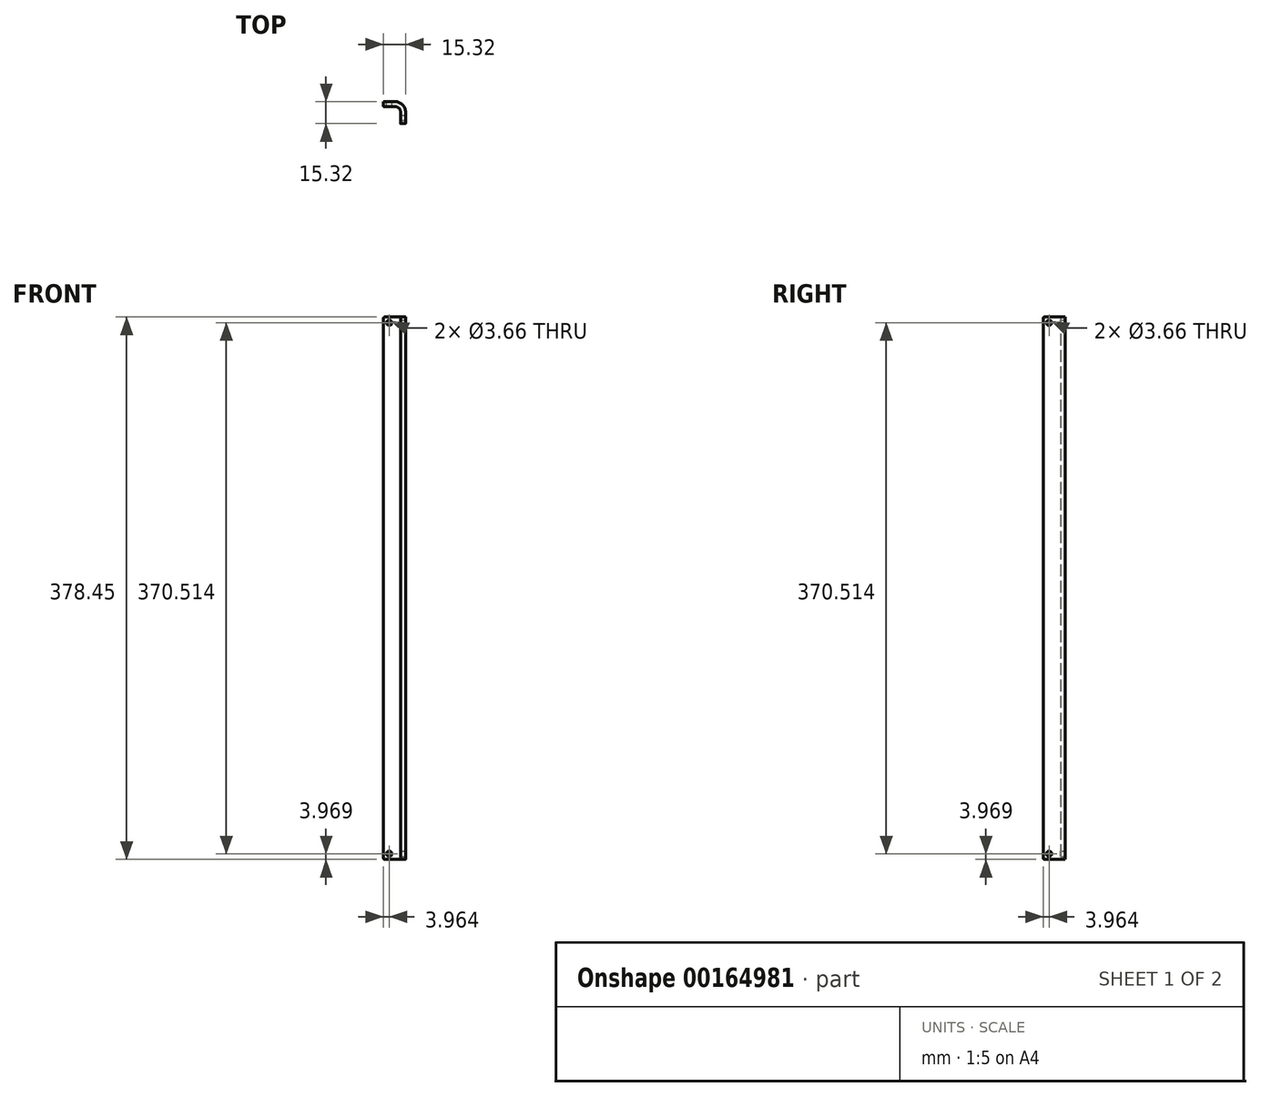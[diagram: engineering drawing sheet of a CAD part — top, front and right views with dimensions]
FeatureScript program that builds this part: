
annotation { "Feature Type Name" : "Feature", "Feature Type Description" : "" }
export const myFeature = defineFeature(function(context is Context, id is Id, definition is map)
    precondition{}
    {
        {
            var Q0;
            Q0=qCreatedBy(makeId("Top.planeOp"),FACE);
            var sketch = newSketch(context, id + "F0", { "sketchPlane" : qUnion([Q0])});
            skLineSegment(sketch, "E0.bottom", {"start": v(0, 0) * mm, "end": v(-11.9, 0) * mm});
            skLineSegment(sketch, "E0.top", {"start": v(3.42, 3.42) * mm, "end": v(-11.9, 3.42) * mm});
            skLineSegment(sketch, "E0.right", {"start": v(-11.9, 0) * mm, "end": v(-11.9, 3.42) * mm});
            skLineSegment(sketch, "E1.top", {"start": v(0, -11.9) * mm, "end": v(3.42, -11.9) * mm});
            skLineSegment(sketch, "E1.left", {"start": v(0, 0) * mm, "end": v(0, -11.9) * mm});
            skLineSegment(sketch, "E1.right", {"start": v(3.42, 3.42) * mm, "end": v(3.42, -11.9) * mm});
            skSolve(sketch);
        }
        {
            var Q0;
            Q0 = qSketchRegion(id + "F0", true);
            extrude(context, id + "F1", {"entities" : qUnion([Q0]), "depth" : 378.45 * mm});
        }
        {
            var Q0;
            Q0=makeQuery(id+"F1.opExtrude","SWEPT_EDGE",EDGE,{"disambiguationData":[OSD([sQuery(id+"F0.wireOp",EDGE,"E0.bottom"),sQuery(id+"F0.wireOp",EDGE,"E1.left")])]});
            fillet(context, id + "F2", {"entities" : qUnion([Q0]), "radius" : 3.97 * mm, "tangentPropagation" : true, "allowEdgeOverflow" : false});
        }
        {
            var Q0;
            Q0=makeQuery(id+"F1.opExtrude","SWEPT_EDGE",EDGE,{"disambiguationData":[OSD([sQuery(id+"F0.wireOp",EDGE,"E0.top"),sQuery(id+"F0.wireOp",EDGE,"E1.right")])]});
            fillet(context, id + "F3", {"entities" : qUnion([Q0]), "radius" : 7.39 * mm, "tangentPropagation" : true, "allowEdgeOverflow" : false});
        }
        {
            var Q0;
            Q0=makeQuery(id+"F1.opExtrude","SWEPT_FACE",FACE,{"disambiguationData":[OSD([sQuery(id+"F0.wireOp",EDGE,"E0.top")])]});
            var sketch = newSketch(context, id + "F4", { "sketchPlane" : qUnion([Q0])});
            skLineSegment(sketch, "E2.bottom", {"start": v(7.94, 378.45) * mm, "end": v(11.9, 378.45) * mm, "construction": true});
            skLineSegment(sketch, "E2.top", {"start": v(7.94, 374.48) * mm, "end": v(11.9, 374.48) * mm, "construction": true});
            skLineSegment(sketch, "E2.left", {"start": v(7.94, 378.45) * mm, "end": v(7.94, 374.48) * mm, "construction": true});
            skLineSegment(sketch, "E2.right", {"start": v(11.9, 378.45) * mm, "end": v(11.9, 374.48) * mm, "construction": true});
            skLineSegment(sketch, "E3.bottom", {"start": v(7.94, 0) * mm, "end": v(11.9, 0) * mm, "construction": true});
            skLineSegment(sketch, "E3.top", {"start": v(7.94, 3.97) * mm, "end": v(11.9, 3.97) * mm, "construction": true});
            skLineSegment(sketch, "E3.left", {"start": v(7.94, 0) * mm, "end": v(7.94, 3.97) * mm, "construction": true});
            skLineSegment(sketch, "E3.right", {"start": v(11.9, 0) * mm, "end": v(11.9, 3.97) * mm, "construction": true});
            skCircle(sketch, "E4", {"center": v(7.94, 3.97) * mm, "radius": 1.83 * mm});
            skCircle(sketch, "E5", {"center": v(7.94, 374.48) * mm, "radius": 1.83 * mm});
            skSolve(sketch);
        }
        {
            var Q0;
            Q0 = qSketchRegion(id + "F4", true);
            var Q1;
            Q1=makeQuery(id+"F1.opExtrude","SWEPT_FACE",FACE,{"disambiguationData":[OSD([sQuery(id+"F0.wireOp",EDGE,"E0.bottom")])]});
            extrude(context, id + "F5", {"entities" : qUnion([Q0]), "operationType" : NewBodyOperationType.REMOVE, "endBound" : BoundingType.UP_TO_SURFACE, "oppositeDirection" : true, "endBoundEntityFace" : qUnion([Q1]), "depth" : 25.4 * mm});
        }
        {
            var Q0;
            Q0=makeQuery(id+"F1.opExtrude","SWEPT_FACE",FACE,{"disambiguationData":[OSD([sQuery(id+"F0.wireOp",EDGE,"E1.right")])]});
            var sketch = newSketch(context, id + "F6", { "sketchPlane" : qUnion([Q0])});
            skLineSegment(sketch, "E6.bottom", {"start": v(-11.9, 378.45) * mm, "end": v(-7.94, 378.45) * mm, "construction": true});
            skLineSegment(sketch, "E6.top", {"start": v(-11.9, 374.48) * mm, "end": v(-7.94, 374.48) * mm, "construction": true});
            skLineSegment(sketch, "E6.left", {"start": v(-11.9, 378.45) * mm, "end": v(-11.9, 374.48) * mm, "construction": true});
            skLineSegment(sketch, "E6.right", {"start": v(-7.94, 378.45) * mm, "end": v(-7.94, 374.48) * mm, "construction": true});
            skLineSegment(sketch, "E7.bottom", {"start": v(-7.94, 0) * mm, "end": v(-11.9, 0) * mm, "construction": true});
            skLineSegment(sketch, "E7.top", {"start": v(-7.94, 3.97) * mm, "end": v(-11.9, 3.97) * mm, "construction": true});
            skLineSegment(sketch, "E7.left", {"start": v(-7.94, 0) * mm, "end": v(-7.94, 3.97) * mm, "construction": true});
            skLineSegment(sketch, "E7.right", {"start": v(-11.9, 0) * mm, "end": v(-11.9, 3.97) * mm, "construction": true});
            skCircle(sketch, "E8", {"center": v(-7.94, 374.48) * mm, "radius": 1.83 * mm});
            skCircle(sketch, "E9", {"center": v(-7.94, 3.97) * mm, "radius": 1.83 * mm});
            skSolve(sketch);
        }
        {
            var Q0;
            Q0 = qSketchRegion(id + "F6", true);
            var Q1;
            Q1=makeQuery(id+"F1.opExtrude","SWEPT_FACE",FACE,{"disambiguationData":[OSD([sQuery(id+"F0.wireOp",EDGE,"E1.left")])]});
            extrude(context, id + "F7", {"entities" : qUnion([Q0]), "operationType" : NewBodyOperationType.REMOVE, "endBound" : BoundingType.UP_TO_SURFACE, "oppositeDirection" : true, "endBoundEntityFace" : qUnion([Q1]), "depth" : 25.4 * mm});
        }
        {
            var Q0;
            Q0=makeQuery(id+"F1.opExtrude","CAP_EDGE",EDGE,{"disambiguationData":[OSD([sQuery(id+"F0.wireOp",EDGE,"E0.right")])],"isStart":false});
            var Q1;
            Q1=makeQuery(id+"F1.opExtrude","CAP_EDGE",EDGE,{"disambiguationData":[OSD([sQuery(id+"F0.wireOp",EDGE,"E1.top")])],"isStart":false});
            var Q2;
            Q2=makeQuery(id+"F1.opExtrude","CAP_EDGE",EDGE,{"disambiguationData":[OSD([sQuery(id+"F0.wireOp",EDGE,"E1.top")])],"isStart":true});
            var Q3;
            Q3=makeQuery(id+"F1.opExtrude","CAP_EDGE",EDGE,{"disambiguationData":[OSD([sQuery(id+"F0.wireOp",EDGE,"E0.right")])],"isStart":true});
            fillet(context, id + "F8", {"entities" : qUnion([Q0, Q1, Q2, Q3]), "radius" : 0.76 * mm, "tangentPropagation" : true, "allowEdgeOverflow" : false});
        }
    });
